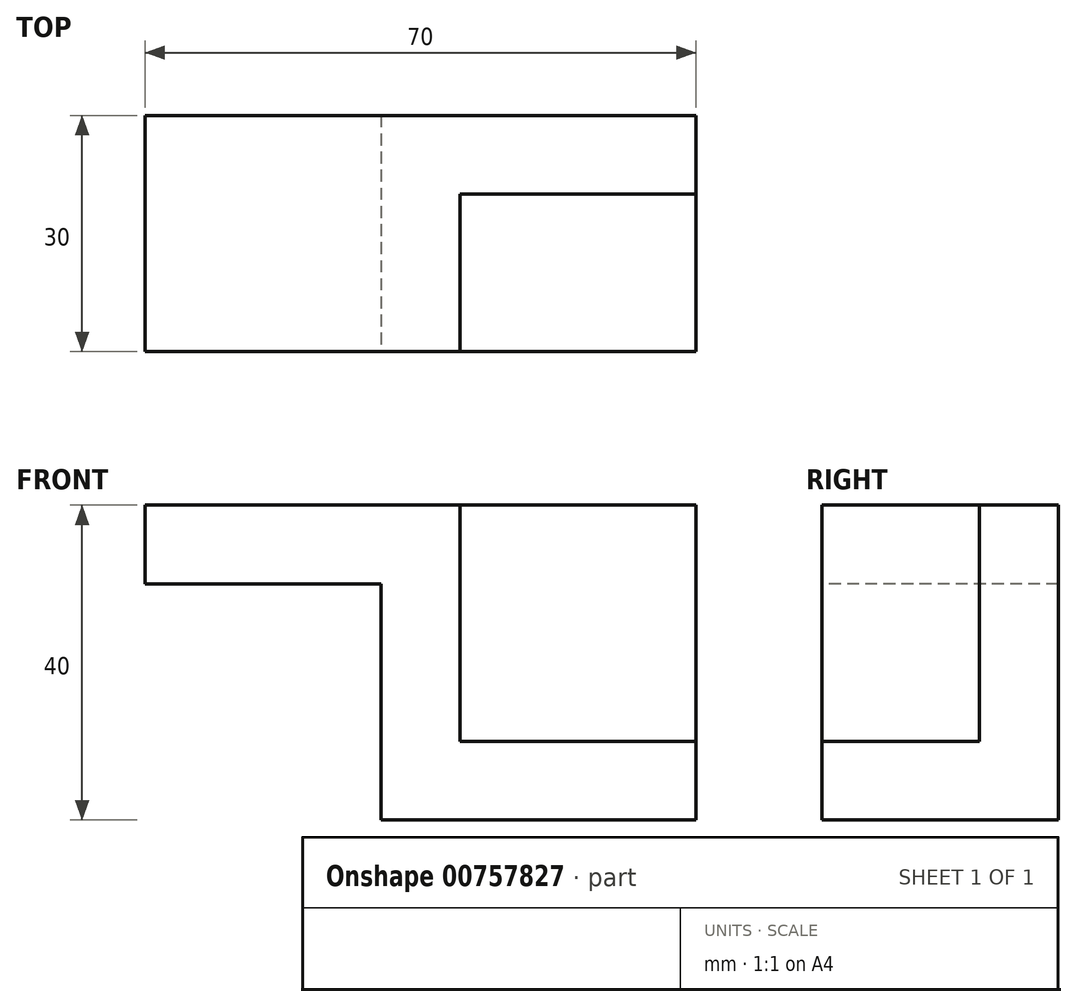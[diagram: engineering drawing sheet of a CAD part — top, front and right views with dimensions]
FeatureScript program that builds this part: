
annotation { "Feature Type Name" : "Feature", "Feature Type Description" : "" }
export const myFeature = defineFeature(function(context is Context, id is Id, definition is map)
    precondition{}
    {
        {
            var Q0;
            Q0=qCreatedBy(makeId("Front.planeOp"),FACE);
            var sketch = newSketch(context, id + "F0", { "sketchPlane" : qUnion([Q0])});
            skLineSegment(sketch, "E0.bottom", {"start": v(0, 0) * mm, "end": v(70, 0) * mm});
            skLineSegment(sketch, "E0.top", {"start": v(0, 40) * mm, "end": v(70, 40) * mm});
            skLineSegment(sketch, "E0.left", {"start": v(0, 0) * mm, "end": v(0, 40) * mm});
            skLineSegment(sketch, "E0.right", {"start": v(70, 0) * mm, "end": v(70, 40) * mm});
            skSolve(sketch);
        }
        {
            var Q0;
            Q0 = qSketchRegion(id + "F0", true);
            extrude(context, id + "F1", {"entities" : qUnion([Q0]), "depth" : 30 * mm, "offsetDistance" : 25 * mm});
        }
        {
            var Q0;
            Q0=makeQuery(id+"F1.opExtrude","CAP_FACE",FACE,{"disambiguationData":[OSD([sQuery(id+"F0.wireOp",EDGE,"E0.bottom"),sQuery(id+"F0.wireOp",EDGE,"E0.top"),sQuery(id+"F0.wireOp",EDGE,"E0.left"),sQuery(id+"F0.wireOp",EDGE,"E0.right")])],"isStart":false});
            var sketch = newSketch(context, id + "F2", { "sketchPlane" : qUnion([Q0])});
            skLineSegment(sketch, "E1.bottom", {"start": v(0, 30) * mm, "end": v(30, 30) * mm});
            skLineSegment(sketch, "E1.top", {"start": v(0, 0) * mm, "end": v(30, 0) * mm});
            skLineSegment(sketch, "E1.left", {"start": v(0, 30) * mm, "end": v(0, 0) * mm});
            skLineSegment(sketch, "E1.right", {"start": v(30, 30) * mm, "end": v(30, 0) * mm});
            skSolve(sketch);
        }
        {
            var Q0;
            Q0=makeQuery(id+"F2.imprint","IMPRINT",FACE,{"disambiguationData":[TD([[makeQuery(id+"F2.imprint","IMPRINT",EDGE,{"derivedFrom":sQuery(id+"F2.wireOp",EDGE,"E1.bottom")}),-1.0]])]});
            extrude(context, id + "F3", {"entities" : qUnion([Q0]), "operationType" : NewBodyOperationType.REMOVE, "endBound" : BoundingType.THROUGH_ALL, "oppositeDirection" : true, "depth" : 25 * mm, "offsetDistance" : 25 * mm});
        }
        {
            var Q0;
            Q0=makeQuery(id+"F1.opExtrude","CAP_FACE",FACE,{"disambiguationData":[OSD([sQuery(id+"F0.wireOp",EDGE,"E0.bottom"),sQuery(id+"F0.wireOp",EDGE,"E0.top"),sQuery(id+"F0.wireOp",EDGE,"E0.left"),sQuery(id+"F0.wireOp",EDGE,"E0.right")])],"isStart":false});
            var sketch = newSketch(context, id + "F4", { "sketchPlane" : qUnion([Q0])});
            skLineSegment(sketch, "E2.bottom", {"start": v(40, 40) * mm, "end": v(70, 40) * mm});
            skLineSegment(sketch, "E2.top", {"start": v(40, 10) * mm, "end": v(70, 10) * mm});
            skLineSegment(sketch, "E2.left", {"start": v(40, 40) * mm, "end": v(40, 10) * mm});
            skLineSegment(sketch, "E2.right", {"start": v(70, 40) * mm, "end": v(70, 10) * mm});
            skSolve(sketch);
        }
        {
            var Q0;
            Q0 = qSketchRegion(id + "F4", true);
            extrude(context, id + "F5", {"entities" : qUnion([Q0]), "operationType" : NewBodyOperationType.REMOVE, "oppositeDirection" : true, "depth" : 20 * mm, "offsetDistance" : 25 * mm});
        }
    });
